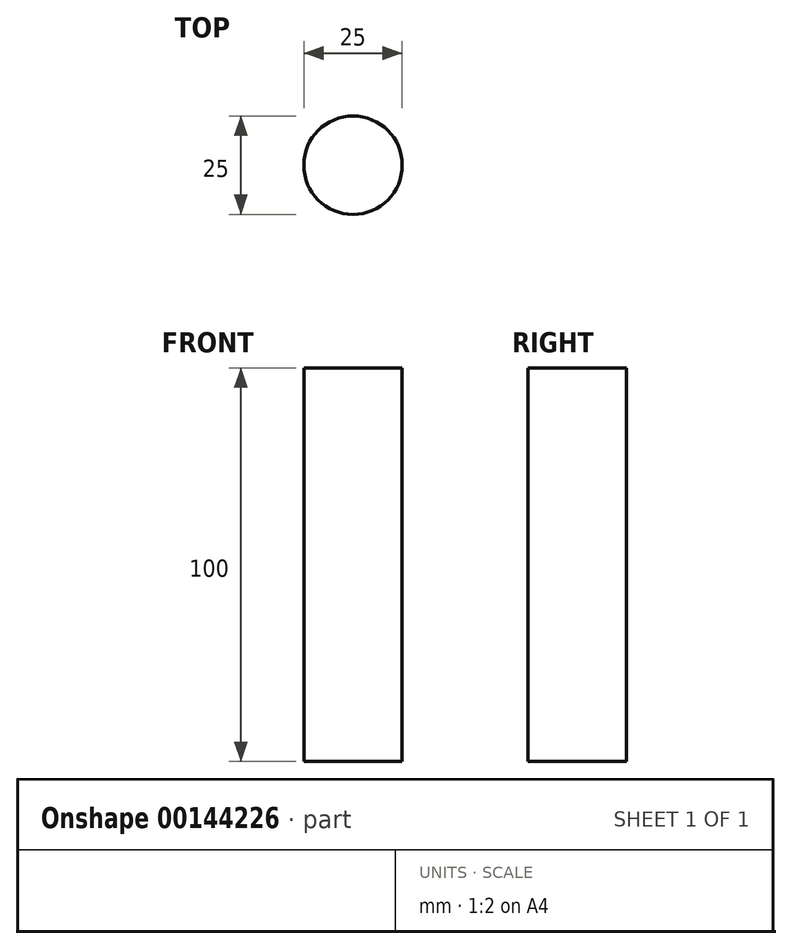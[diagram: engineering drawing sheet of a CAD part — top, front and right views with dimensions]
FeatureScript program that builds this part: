
annotation { "Feature Type Name" : "Feature", "Feature Type Description" : "" }
export const myFeature = defineFeature(function(context is Context, id is Id, definition is map)
    precondition{}
    {
        {
            var Q0;
            Q0=qCreatedBy(makeId("Top.planeOp"),FACE);
            var sketch = newSketch(context, id + "F0", { "sketchPlane" : qUnion([Q0])});
            skCircle(sketch, "E0", {"center": v(0, 0) * mm, "radius": 12.5 * mm});
            skSolve(sketch);
        }
        {
            var Q0;
            Q0=makeQuery(id+"F0.imprint","IMPRINT",FACE,{"disambiguationData":[TD([[makeQuery(id+"F0.imprint","IMPRINT",EDGE,{"derivedFrom":sQuery(id+"F0.wireOp",EDGE,"E0")}),1.0]])]});
            extrude(context, id + "F1", {"entities" : qUnion([Q0]), "depth" : 100 * mm});
        }
    });
